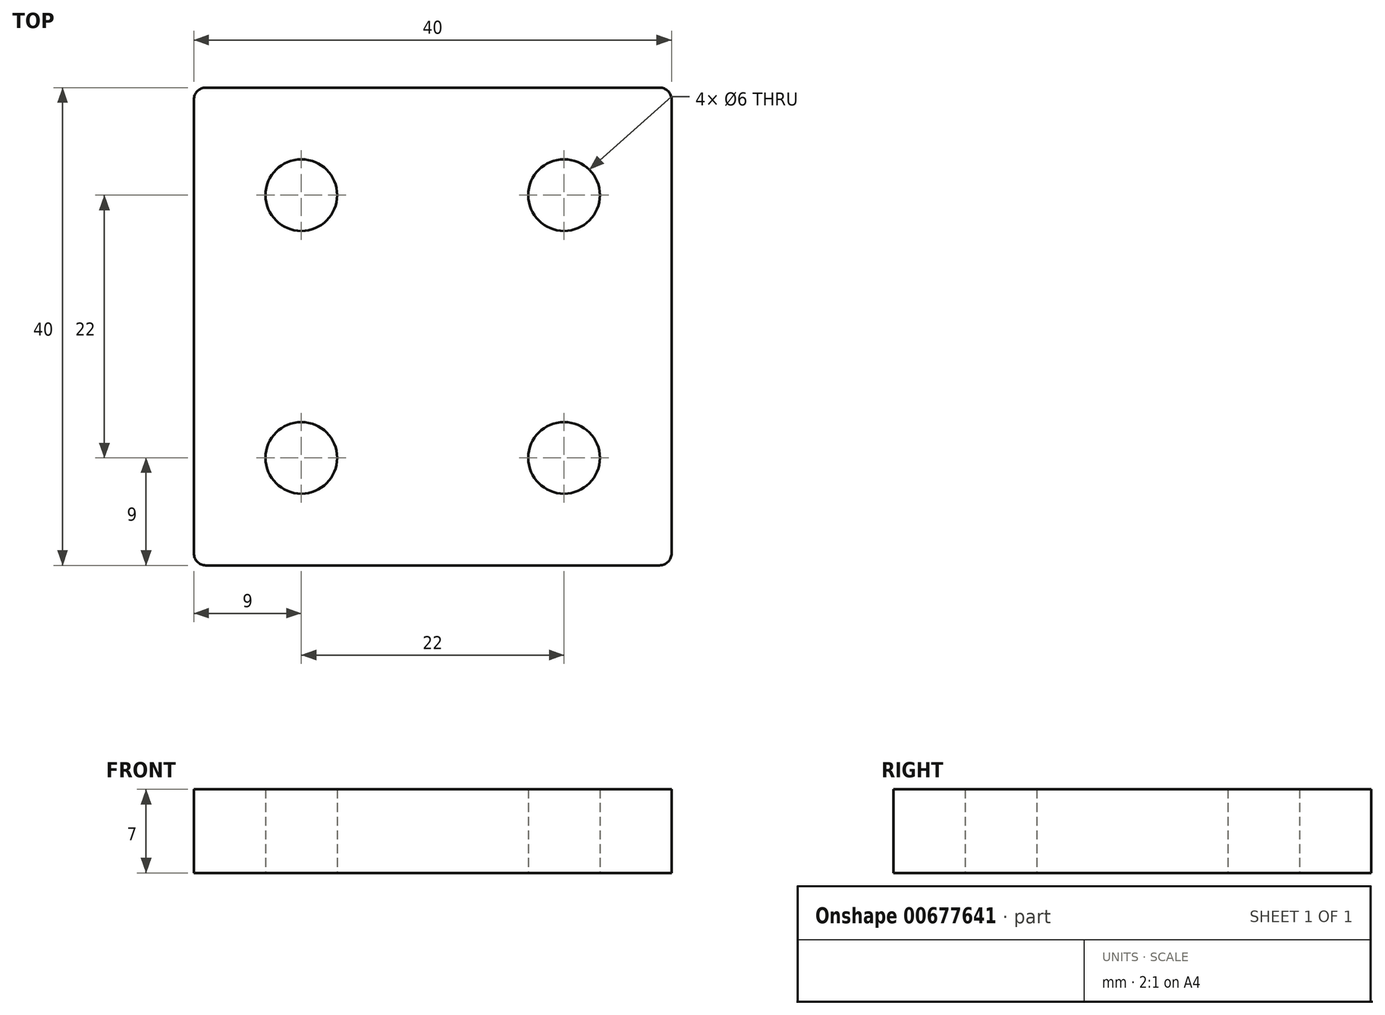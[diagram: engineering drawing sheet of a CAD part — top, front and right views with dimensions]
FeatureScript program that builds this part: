
annotation { "Feature Type Name" : "Feature", "Feature Type Description" : "" }
export const myFeature = defineFeature(function(context is Context, id is Id, definition is map)
    precondition{}
    {
        {
            var Q0;
            Q0=qCreatedBy(makeId("Top.planeOp"),FACE);
            var sketch = newSketch(context, id + "F0", { "sketchPlane" : qUnion([Q0])});
            skLineSegment(sketch, "E0.bottom", {"start": v(0, 0) * mm, "end": v(40, 0) * mm});
            skLineSegment(sketch, "E0.top", {"start": v(0, 40) * mm, "end": v(40, 40) * mm});
            skLineSegment(sketch, "E0.left", {"start": v(0, 0) * mm, "end": v(0, 40) * mm});
            skLineSegment(sketch, "E0.right", {"start": v(40, 0) * mm, "end": v(40, 40) * mm});
            skCircle(sketch, "E1", {"center": v(31, 9) * mm, "radius": 3 * mm});
            skCircle(sketch, "E2.0.1.0", {"center": v(31, 31) * mm, "radius": 3 * mm});
            skCircle(sketch, "E2.1.0.0", {"center": v(9, 9) * mm, "radius": 3 * mm});
            skCircle(sketch, "E2.1.1.0", {"center": v(9, 31) * mm, "radius": 3 * mm});
            skLineSegment(sketch, "E2.direction1", {"start": v(31, 9) * mm, "end": v(9, 9) * mm, "construction": true});
            skLineSegment(sketch, "E2.direction2", {"start": v(31, 9) * mm, "end": v(31, 31) * mm, "construction": true});
            skSolve(sketch);
        }
        {
            var Q0;
            Q0=makeQuery(id+"F0.imprint","IMPRINT",FACE,{"disambiguationData":[TD([[makeQuery(id+"F0.imprint","IMPRINT",EDGE,{"derivedFrom":sQuery(id+"F0.wireOp",EDGE,"E0.bottom")}),1.0]])]});
            extrude(context, id + "F1", {"entities" : qUnion([Q0]), "depth" : 7 * mm, "offsetDistance" : 25 * mm});
        }
        {
            var Q0;
            Q0=makeQuery(id+"F1.opExtrude","SWEPT_EDGE",EDGE,{"disambiguationData":[OSD([sQuery(id+"F0.wireOp",EDGE,"E0.bottom"),sQuery(id+"F0.wireOp",EDGE,"E0.right")])]});
            var Q1;
            Q1=makeQuery(id+"F1.opExtrude","SWEPT_EDGE",EDGE,{"disambiguationData":[OSD([sQuery(id+"F0.wireOp",EDGE,"E0.top"),sQuery(id+"F0.wireOp",EDGE,"E0.right")])]});
            var Q2;
            Q2=makeQuery(id+"F1.opExtrude","SWEPT_EDGE",EDGE,{"disambiguationData":[OSD([sQuery(id+"F0.wireOp",EDGE,"E0.bottom"),sQuery(id+"F0.wireOp",EDGE,"E0.left")])]});
            var Q3;
            Q3=makeQuery(id+"F1.opExtrude","SWEPT_EDGE",EDGE,{"disambiguationData":[OSD([sQuery(id+"F0.wireOp",EDGE,"E0.top"),sQuery(id+"F0.wireOp",EDGE,"E0.left")])]});
            fillet(context, id + "F2", {"entities" : qUnion([Q0, Q1, Q2, Q3]), "radius" : 1 * mm, "tangentPropagation" : true, "allowEdgeOverflow" : false});
        }
    });
